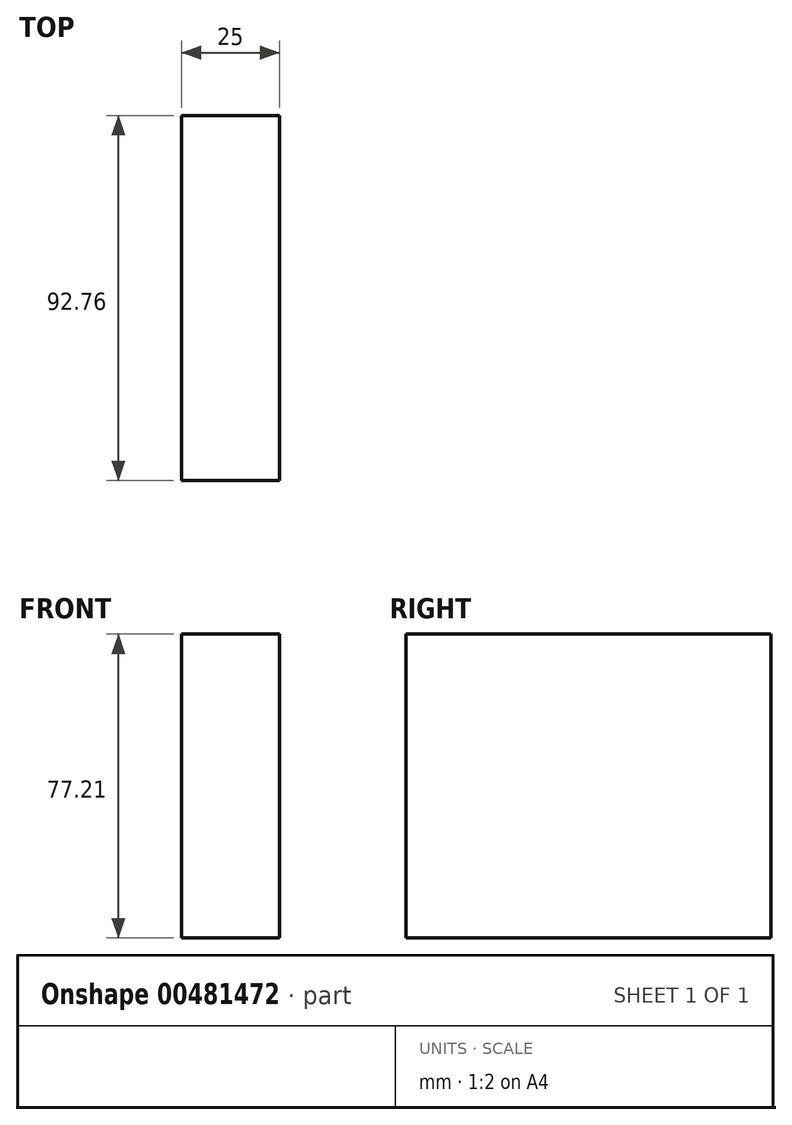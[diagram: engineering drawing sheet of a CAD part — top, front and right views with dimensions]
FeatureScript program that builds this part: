
annotation { "Feature Type Name" : "Feature", "Feature Type Description" : "" }
export const myFeature = defineFeature(function(context is Context, id is Id, definition is map)
    precondition{}
    {
        {
            var Q0;
            Q0=qCreatedBy(makeId("Right.planeOp"),FACE);
            var sketch = newSketch(context, id + "F0", { "sketchPlane" : qUnion([Q0])});
            skLineSegment(sketch, "E0.bottom", {"start": v(-100.63, 90.23) * mm, "end": v(-7.87, 90.23) * mm});
            skLineSegment(sketch, "E0.top", {"start": v(-100.63, 13.02) * mm, "end": v(-7.87, 13.02) * mm});
            skLineSegment(sketch, "E0.left", {"start": v(-100.63, 90.23) * mm, "end": v(-100.63, 13.02) * mm});
            skLineSegment(sketch, "E0.right", {"start": v(-7.87, 90.23) * mm, "end": v(-7.87, 13.02) * mm});
            skSolve(sketch);
        }
        {
            var Q0;
            Q0 = qSketchRegion(id + "F0", true);
            extrude(context, id + "F1", {"entities" : qUnion([Q0]), "depth" : 25 * mm});
        }
    });
